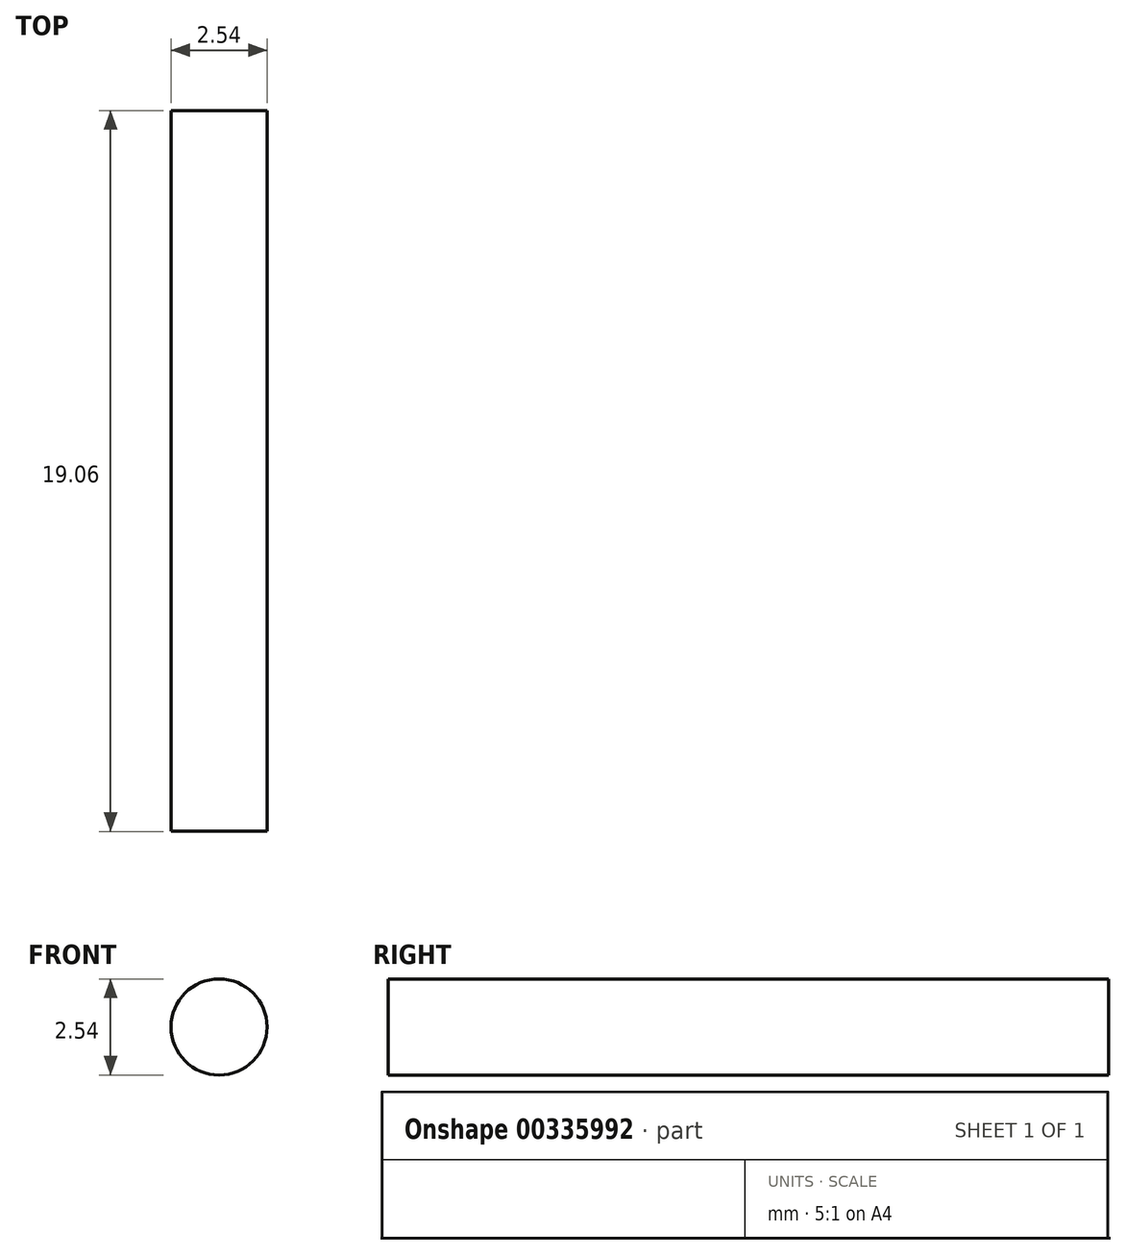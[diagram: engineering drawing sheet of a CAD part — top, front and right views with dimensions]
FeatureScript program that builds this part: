
annotation { "Feature Type Name" : "Feature", "Feature Type Description" : "" }
export const myFeature = defineFeature(function(context is Context, id is Id, definition is map)
    precondition{}
    {
        {
            var Q0;
            Q0=qCreatedBy(makeId("Front.planeOp"),FACE);
            var sketch = newSketch(context, id + "F0", { "sketchPlane" : qUnion([Q0])});
            skCircle(sketch, "E0", {"center": v(0, 0) * mm, "radius": 1.27 * mm});
            skSolve(sketch);
        }
        {
            var Q0;
            Q0=makeQuery(id+"F0.imprint","IMPRINT",FACE,{"disambiguationData":[TD([[makeQuery(id+"F0.imprint","IMPRINT",EDGE,{"derivedFrom":sQuery(id+"F0.wireOp",EDGE,"E0")}),1.0]])]});
            extrude(context, id + "F1", {"entities" : qUnion([Q0]), "endBound" : BoundingType.SYMMETRIC, "depth" : 19.05 * mm});
        }
    });
